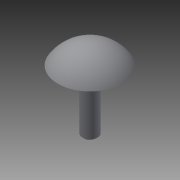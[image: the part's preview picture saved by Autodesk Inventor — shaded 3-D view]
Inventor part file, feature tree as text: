
AUTODESK INVENTOR PART (.ipt)
format: ipt  version: 2015 (Build 190159000, 159)  size: 97,280 bytes
history: native  units: in
note: dims shown in document units (in); Inventor stores cm internally (conversion verified against a paired STEP export)
features: revolve x1, chamfer x1, sketch x1
ambient origin geometry x8: Origin, YZ Plane, XZ Plane, XY Plane, X Axis, Y Axis, Z Axis, Center Point
bodies: Solid1 (feature_tree)
feature tree (3):
  revolve  "Revolution1"  [1 undecoded]
  chamfer  "Chamfer1"  Distance=0.325in
  sketch  "Sketch1"  dims[d0=0.1562in d1=0.25in d2=0.325in d3=0.0312in d4=0.1in d5=90.0deg d6=0.01in d7=0.125in d8=45.0deg]
note: 1 required parameter value undecoded (feature->parameter linkage not recoverable at this tier; creation-order binding heuristic only, values carry confidence <= 0.55)
